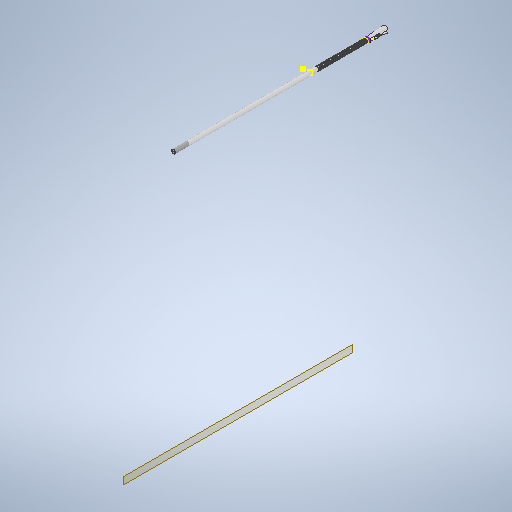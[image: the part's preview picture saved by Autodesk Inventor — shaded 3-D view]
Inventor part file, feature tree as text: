
AUTODESK INVENTOR PART (.ipt)
format: ipt  version: 2025.2 (Build 292293000, 293)  size: 935,936 bytes
history: native  units: mm
features: sketch x31, extrude x20, plane x5, loft x1, thread x1, other x1
ambient origin geometry x8: Origin, YZ Plane, XZ Plane, XY Plane, X Axis, Y Axis, Z Axis, Center Point
bodies: Solid1 (feature_tree)
feature tree (59):
  extrude  "Extrusion1"  Depth=40.0mm TaperAngle=0.0deg
  plane  "Work Plane1"
  extrude  "Extrusion2"  Depth=1.3mm
  extrude  "Extrusion3"  Depth=0.5mm
  extrude  "Extrusion4"  Depth=40.0mm
  sketch  "Sketch5"  dims[d11=0.3mm d12=0.3mm]
  extrude  "Extrusion5"  Depth=0.3mm
  extrude  "Extrusion6"  Depth=0.3mm
  extrude  "Extrusion7"  Depth=0.6mm
  extrude  "Extrusion8"  Depth=0.6mm
  plane  "Work Plane2"
  extrude  "Extrusion9"  Depth=40.0mm TaperAngle=360.0deg
  extrude  "Extrusion10"  Depth=0.6mm TaperAngle=0.0deg
  sketch  "Sketch12"  dims[d39=4.0mm d40=0.1mm]
  sketch  "Sketch13"  dims[d41=20.75mm d42=0.0mm d43=0.2mm]
  extrude  "Extrusion11"  Depth=0.6mm TaperAngle=0.0deg
  sketch  "Sketch16"  dims[d48=0.25mm d51=0.75mm]
  sketch  "Sketch17"  dims[d52=0.2mm d53=0.2mm]
  sketch  "Sketch18"  dims[d54=2.591063mm d55=0.5mm]
  extrude  "Extrusion13"  [1 undecoded]
  extrude  "Extrusion14"  Depth=0.1mm
  extrude  "Extrusion18"  Depth=0.2mm
  extrude  "Extrusion19"  Depth=2.0mm
  extrude  "Extrusion20"  Depth=0.75mm
  plane  "Work Plane3"
  sketch  "Sketch38"  dims[d68=1.0mm]
  sketch  "Sketch39"  dims[d69=99.0mm d70=0.0mm]
  loft  "Loft3"
  plane  "Work Plane4"
  extrude  "Extrusion21"  Depth=0.5mm
  sketch  "Sketch43"  dims[d74=4.5mm]
  extrude  "Extrusion23"  Depth=0.2mm
  sketch  "Sketch48"  dims[d95=1.5mm d96=0.0mm]
  sketch  "Sketch49"  dims[d97=0.6mm]
  plane  "Work Plane5"
  extrude  "Extrusion24"  Depth=2.5mm
  extrude  "Extrusion25"  Depth=20.754mm TaperAngle=0.0deg
  thread  "Thread1"  [1 undecoded]
  sketch  "Sketch1"  dims[d0=3.0mm d1=40.0mm d2=0.0mm]
  sketch  "Sketch2"  dims[d5=0.5mm d6=0.5mm]
  sketch  "Sketch3"  dims[d7=0.6mm d8=40.0mm]
  sketch  "Sketch4"  dims[d9=0.3mm d10=0.3mm]
  sketch  "Sketch Circular Pattern1"  dims[d3=-40.0mm d4=1.3mm]
  sketch  "Sketch6"  dims[d13=54.75mm d14=5.0mm d15=0.0mm d16=0.0mm d17=0.6mm]
  sketch  "Sketch7"  dims[d20=54.75mm d21=0.0mm d22=0.6mm]
  sketch  "Sketch8"  dims[d23=2.3mm d24=40.0mm d26=360.0deg]
  sketch  "Sketch9"  dims[d28=54.75mm d29=0.0mm d30=0.6mm d31=0.0mm]
  sketch  "Sketch10"  dims[d32=0.6mm d33=0.0mm d34=0.6mm d35=0.0mm]
  sketch  "Sketch11"  dims[d36=10.0mm d37=0.0mm d38=-13.25mm]
  sketch  "Sketch14"  dims[d44=0.5mm d45=2.0mm]
  sketch  "Sketch19"  dims[d56=0.1mm d57=0.2mm]
  sketch  "Sketch21"  dims[d58=0.25mm d59=2.5mm]
  sketch  "Sketch36"  dims[d60=2.5mm d61=20.754mm d62=0.0mm d63=46.004mm d64=0.0mm]
  sketch  "Sketch37"  dims[d67=1.0mm]
  other  "Edges3"
  sketch  "Sketch40"  dims[d71=4.0mm d72=0.0mm]
  sketch  "Sketch44"  dims[d93=8.0mm d94=0.0mm]
  sketch  "Sketch50"  dims[d98=1.5mm d99=0.0mm]
  sketch  "Sketch51"  dims[d100=55.0mm d101=4.75mm d102=0.0mm d103=90.0deg d104=0.0mm d105=90.0deg d106=-5.0mm d107=2.25mm d108=7.0mm d109=13.75mm d110=0.0mm d128=100.0mm d129=0.0mm d130=0.25mm d133=-1.75mm d134=0.3mm d136=0.3mm d137=0.3mm d138=0.3mm d139=0.3mm d140=0.3mm d141=0.15mm d142=0.15mm d143=3.5mm d144=0.0mm d145=0.4mm d146=0.2mm d147=0.2mm d148=3.407915mm d149=0.02618mm d150=145.25mm d151=0.0mm d152=10.0mm d153=0.0mm d73=0.5mm d79=0.5mm d80=0.872665mm d81=0.5mm d82=0.872665mm d91=0.5mm d92=0.872665mm d126=0.5mm d127=0.872665mm]
note: 2 required parameter values undecoded (feature->parameter linkage not recoverable at this tier; creation-order binding heuristic only, values carry confidence <= 0.55)
